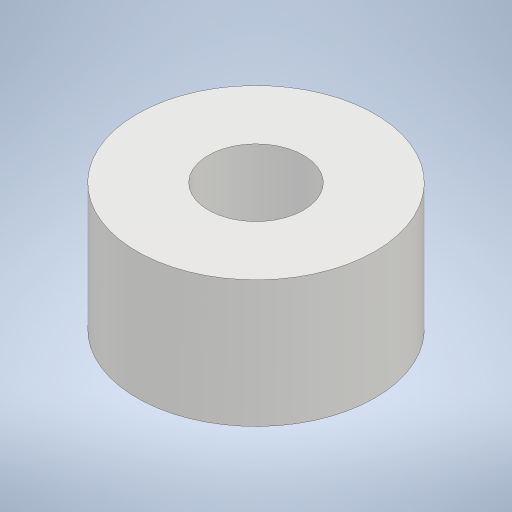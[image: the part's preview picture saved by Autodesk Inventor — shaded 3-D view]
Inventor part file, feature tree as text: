
AUTODESK INVENTOR PART (.ipt)
format: ipt  version: 2023 (Build 270158030, 158C)  size: 293,376 bytes
history: native  units: mm
features: other x1, extrude x1, sketch x1
ambient origin geometry x8: Origin, YZ Plane, XZ Plane, XY Plane, X Axis, Y Axis, Z Axis, Center Point
bodies: Body1 (feature_tree)
feature tree (3):
  other  "ソリッド1"
  extrude  "押し出し1"  Depth=6.0mm
  sketch  "スケッチ1"
